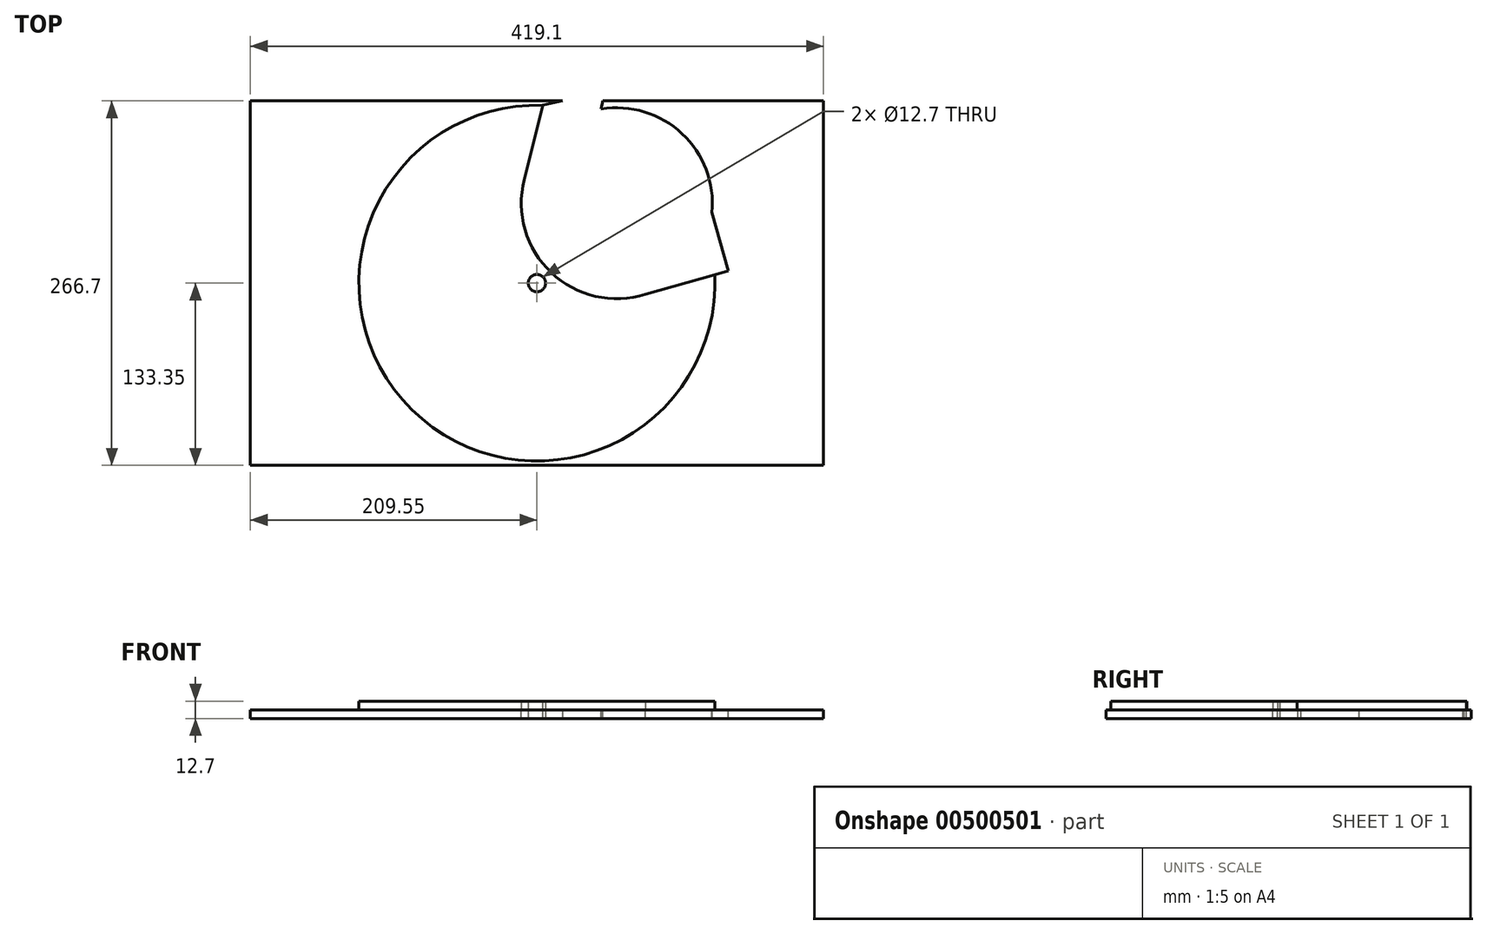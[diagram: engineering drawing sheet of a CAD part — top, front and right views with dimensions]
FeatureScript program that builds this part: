
annotation { "Feature Type Name" : "Feature", "Feature Type Description" : "" }
export const myFeature = defineFeature(function(context is Context, id is Id, definition is map)
    precondition{}
    {
        {
            var Q0;
            Q0=qCreatedBy(makeId("Top.planeOp"),FACE);
            var sketch = newSketch(context, id + "F0", { "sketchPlane" : qUnion([Q0])});
            skLineSegment(sketch, "E0.bottom", {"start": v(-209.55, 133.35) * mm, "end": v(209.55, 133.35) * mm});
            skLineSegment(sketch, "E0.top", {"start": v(-209.55, -133.35) * mm, "end": v(209.55, -133.35) * mm});
            skLineSegment(sketch, "E0.left", {"start": v(-209.55, 133.35) * mm, "end": v(-209.55, -133.35) * mm});
            skLineSegment(sketch, "E0.right", {"start": v(209.55, 133.35) * mm, "end": v(209.55, -133.35) * mm});
            skCircle(sketch, "E1", {"center": v(0, 0) * mm, "radius": 6.35 * mm});
            skPoint(sketch, "E2", {"position": v(209.55, 0) * mm});
            skPoint(sketch, "E3", {"position": v(0, 133.35) * mm});
            skSolve(sketch);
        }
        {
            var Q0;
            Q0=makeQuery(id+"F0.imprint","IMPRINT",FACE,{"disambiguationData":[TD([[makeQuery(id+"F0.imprint","IMPRINT",EDGE,{"derivedFrom":sQuery(id+"F0.wireOp",EDGE,"E0.bottom")}),-1.0]])]});
            extrude(context, id + "F1", {"entities" : qUnion([Q0]), "depth" : 6.35 * mm});
        }
        {
            var Q0;
            Q0=makeQuery(id+"F1.opExtrude","CAP_FACE",FACE,{"disambiguationData":[OSD([sQuery(id+"F0.wireOp",EDGE,"E0.bottom"),sQuery(id+"F0.wireOp",EDGE,"E0.top"),sQuery(id+"F0.wireOp",EDGE,"E0.left"),sQuery(id+"F0.wireOp",EDGE,"E0.right"),sQuery(id+"F0.wireOp",EDGE,"E1")])],"isStart":false});
            var sketch = newSketch(context, id + "F2", { "sketchPlane" : qUnion([Q0])});
            skCircle(sketch, "E4", {"center": v(58.42, 58.42) * mm, "radius": 69.85 * mm});
            skSolve(sketch);
        }
        {
            var Q0;
            Q0=makeQuery(id+"F2.imprint","IMPRINT",FACE,{"disambiguationData":[TD([[makeQuery(id+"F2.imprint","IMPRINT",EDGE,{"derivedFrom":sQuery(id+"F2.wireOp",EDGE,"E4")}),1.0]])]});
            extrude(context, id + "F3", {"entities" : qUnion([Q0]), "operationType" : NewBodyOperationType.REMOVE, "endBound" : BoundingType.UP_TO_NEXT, "oppositeDirection" : true, "depth" : 25.4 * mm});
        }
        {
            var Q0;
            Q0=makeQuery(id+"F1.opExtrude","CAP_FACE",FACE,{"disambiguationData":[OSD([sQuery(id+"F0.wireOp",EDGE,"E0.bottom"),sQuery(id+"F0.wireOp",EDGE,"E0.top"),sQuery(id+"F0.wireOp",EDGE,"E0.left"),sQuery(id+"F0.wireOp",EDGE,"E0.right"),sQuery(id+"F0.wireOp",EDGE,"E1")])],"isStart":false});
            var sketch = newSketch(context, id + "F4", { "sketchPlane" : qUnion([Q0])});
            skCircle(sketch, "E5", {"center": v(0, 0) * mm, "radius": 130.18 * mm});
            skCircle(sketch, "E6", {"center": v(0, 0) * mm, "radius": 6.35 * mm});
            skSolve(sketch);
        }
        {
            var Q0;
            Q0=makeQuery(id+"F4.imprint","IMPRINT",FACE,{"disambiguationData":[TD([[makeQuery(id+"F4.imprint","IMPRINT",EDGE,{"derivedFrom":sQuery(id+"F4.wireOp",EDGE,"E6")}),-1.0]])]});
            var Q1;
            {var subQ0=sQuery(id+"F4.wireOp",EDGE,"E5");var subQ1=makeQuery(id+"F3.boolean.opBoolean","COPY",EDGE,{"derivedFrom":makeQuery(id+"F3.opExtrude","CAP_EDGE",EDGE,{"disambiguationData":[OSD([sQuery(id+"F2.wireOp",EDGE,"E4")])],"isStart":true})});var subQ2=makeQuery(id+"F4.imprint","INTERSECT",VERTEX,{"disambiguationData":[OD(0.0)],"derivedFrom":[subQ1,subQ0]});Q1=makeQuery(id+"F4.imprint","IMPRINT",FACE,{"disambiguationData":[TD([[makeQuery(id+"F4.imprint","IMPRINT",EDGE,{"disambiguationData":[TD([[subQ2,1.0]])],"derivedFrom":subQ0}),1.0]])]});}
            extrude(context, id + "F5", {"entities" : qUnion([Q0, Q1]), "depth" : 6.35 * mm});
        }
        {
            var Q0;
            Q0=makeQuery(id+"F2.imprint","IMPRINT",FACE,{"disambiguationData":[TD([[makeQuery(id+"F2.imprint","IMPRINT",EDGE,{"derivedFrom":sQuery(id+"F2.wireOp",EDGE,"E4")}),1.0]])]});
            extrude(context, id + "F6", {"entities" : qUnion([Q0]), "operationType" : NewBodyOperationType.REMOVE, "depth" : 25.4 * mm});
        }
        {
            var Q0;
            Q0=makeQuery(id+"F5.opExtrude","CAP_FACE",FACE,{"disambiguationData":[OSD([sQuery(id+"F4.wireOp",EDGE,"E5"),sQuery(id+"F4.wireOp",EDGE,"E6")])],"isStart":false});
            var sketch = newSketch(context, id + "F7", { "sketchPlane" : qUnion([Q0])});
            skLineSegment(sketch, "E7", {"start": v(-9.25, 75.73) * mm, "end": v(4.27, 130.1) * mm});
            skLineSegment(sketch, "E8", {"start": v(4.27, 130.1) * mm, "end": v(49.26, 140.27) * mm});
            skLineSegment(sketch, "E9", {"start": v(49.26, 140.27) * mm, "end": v(36.84, 65.85) * mm});
            skLineSegment(sketch, "E10", {"start": v(36.84, 65.85) * mm, "end": v(-9.25, 75.73) * mm});
            skLineSegment(sketch, "E11", {"start": v(75.52, -9.3) * mm, "end": v(140.07, 9.03) * mm});
            skPoint(sketch, "E11.endSnap0", {"position": v(9.03, 9.03) * mm});
            skLineSegment(sketch, "E12", {"start": v(140.07, 9.03) * mm, "end": v(127.25, 54.15) * mm});
            skLineSegment(sketch, "E13", {"start": v(127.25, 54.15) * mm, "end": v(75.52, -9.3) * mm});
            skSolve(sketch);
        }
        {
            var Q0;
            {var subQ4=sQuery(id+"F7.wireOp",EDGE,"E8");Q0=makeQuery(id+"F7.imprint","IMPRINT",FACE,{"disambiguationData":[TD([[makeQuery(id+"F7.imprint","IMPRINT",EDGE,{"derivedFrom":subQ4}),-1.0]])]});}
            var Q1;
            {var subQ0=sQuery(id+"F7.wireOp",EDGE,"E7");Q1=makeQuery(id+"F7.imprint","IMPRINT",FACE,{"disambiguationData":[TD([[makeQuery(id+"F7.imprint","IMPRINT",EDGE,{"derivedFrom":subQ0}),-1.0]])]});}
            var Q2;
            {var subQ1=sQuery(id+"F7.wireOp",EDGE,"E12");Q2=makeQuery(id+"F7.imprint","IMPRINT",FACE,{"disambiguationData":[TD([[makeQuery(id+"F7.imprint","IMPRINT",EDGE,{"derivedFrom":subQ1}),1.0]])]});}
            var Q3;
            {var subQ0=sQuery(id+"F7.wireOp",EDGE,"E11");var subQ1=sQuery(id+"F4.wireOp",EDGE,"E5");var subQ2=makeQuery(id+"F5.opExtrude","CAP_EDGE",EDGE,{"disambiguationData":[OSD([subQ1])],"isStart":false});var subQ3=makeQuery(id+"F7.imprint","INTERSECT",VERTEX,{"derivedFrom":[subQ2,subQ0]});Q3=makeQuery(id+"F7.imprint","IMPRINT",FACE,{"disambiguationData":[TD([[makeQuery(id+"F7.imprint","IMPRINT",EDGE,{"disambiguationData":[TD([[subQ3,1.0]])],"derivedFrom":subQ0}),1.0]])]});}
            extrude(context, id + "F8", {"entities" : qUnion([Q0, Q1, Q2, Q3]), "operationType" : NewBodyOperationType.REMOVE, "oppositeDirection" : true, "depth" : 25.4 * mm});
        }
    });
